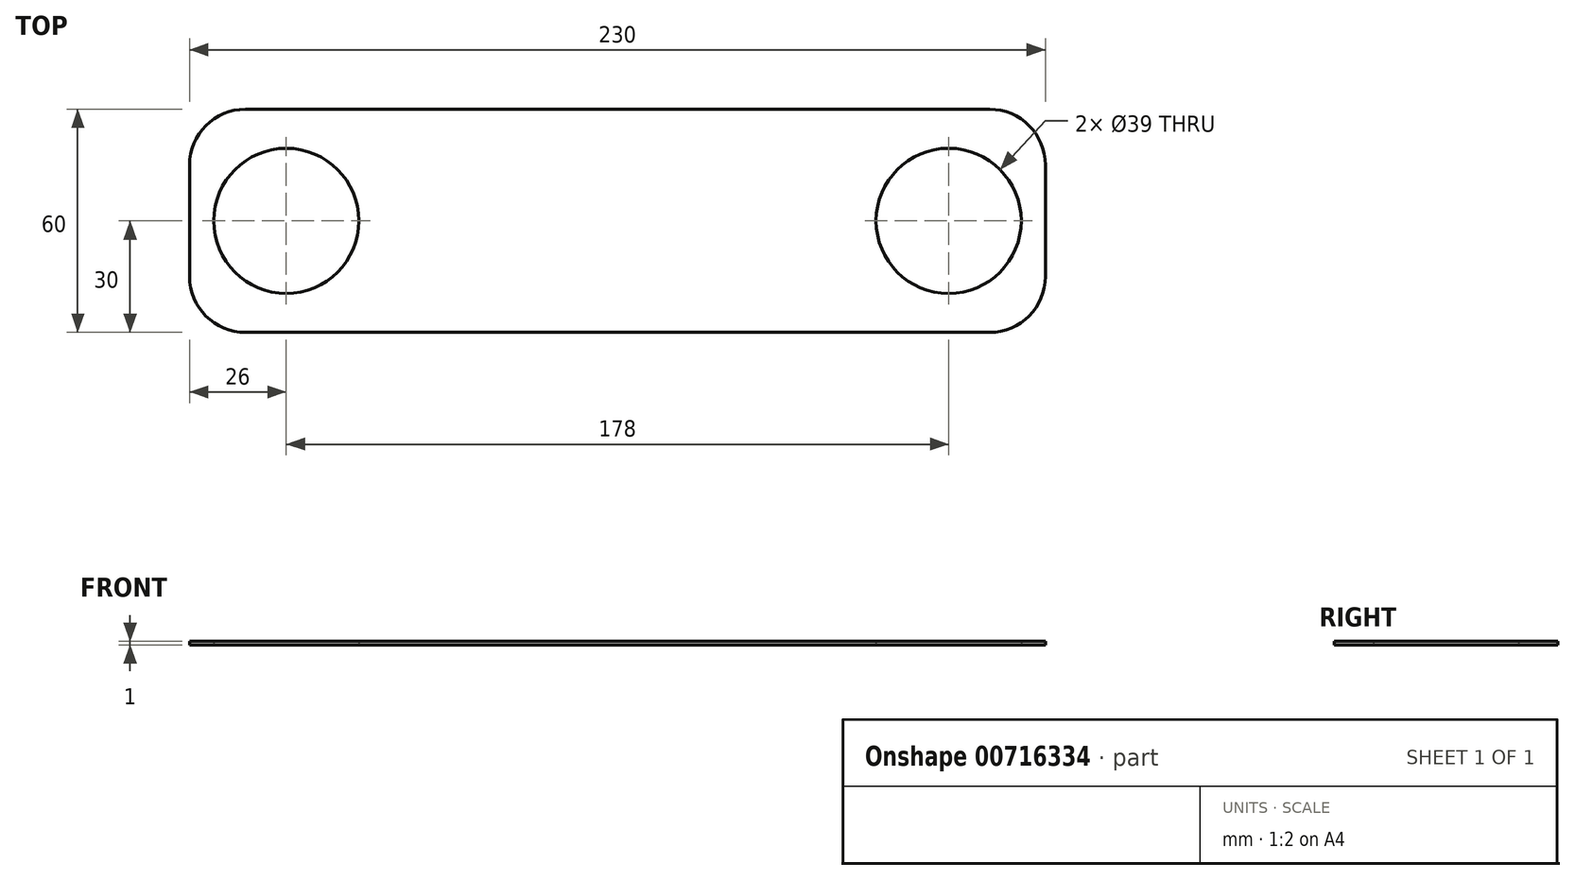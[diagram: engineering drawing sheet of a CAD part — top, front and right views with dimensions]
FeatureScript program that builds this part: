
annotation { "Feature Type Name" : "Feature", "Feature Type Description" : "" }
export const myFeature = defineFeature(function(context is Context, id is Id, definition is map)
    precondition{}
    {
        {
            var Q0;
            Q0=qCreatedBy(makeId("Top.planeOp"),FACE);
            var sketch = newSketch(context, id + "F0", { "sketchPlane" : qUnion([Q0])});
            skLineSegment(sketch, "E0.bottom", {"start": v(100, -30) * mm, "end": v(-100, -30) * mm});
            skLineSegment(sketch, "E0.top", {"start": v(100, 30) * mm, "end": v(-100, 30) * mm});
            skLineSegment(sketch, "E0.left", {"start": v(115, -15) * mm, "end": v(115, 15) * mm});
            skLineSegment(sketch, "E0.right", {"start": v(-115, -15) * mm, "end": v(-115, 15) * mm});
            skPoint(sketch, "E0.middle", {"position": v(0, 0) * mm});
            skLineSegment(sketch, "E1", {"start": v(0, 0) * mm, "end": v(-98.84, 0) * mm, "construction": true});
            skPoint(sketch, "E1.endSnap0", {"position": v(-89, 0) * mm});
            skLineSegment(sketch, "E2", {"start": v(-98.84, 0) * mm, "end": v(125.7, 0) * mm, "construction": true});
            skPoint(sketch, "E3.visualSharp", {"position": v(-115, 30) * mm});
            skArc(sketch, "E3.filletArc", {"start": v(-100, 30) * mm, "mid": v(-110.6, 25.6) * mm, "end": v(-115, 15) * mm});
            skPoint(sketch, "E4.visualSharp", {"position": v(-115, -30) * mm});
            skArc(sketch, "E4.filletArc", {"start": v(-115, -15) * mm, "mid": v(-110.6, -25.6) * mm, "end": v(-100, -30) * mm});
            skPoint(sketch, "E5.visualSharp", {"position": v(115, 30) * mm});
            skArc(sketch, "E5.filletArc", {"start": v(115, 15) * mm, "mid": v(110.6, 25.6) * mm, "end": v(100, 30) * mm});
            skPoint(sketch, "E6.visualSharp", {"position": v(115, -30) * mm});
            skArc(sketch, "E6.filletArc", {"start": v(100, -30) * mm, "mid": v(110.6, -25.6) * mm, "end": v(115, -15) * mm});
            skCircle(sketch, "E7", {"center": v(-89, 0) * mm, "radius": 19.5 * mm});
            skCircle(sketch, "E8", {"center": v(89, 0) * mm, "radius": 19.5 * mm});
            skSolve(sketch);
        }
        {
            var Q0;
            Q0 = qSketchRegion(id + "F0", true);
            extrude(context, id + "F1", {"entities" : qUnion([Q0]), "depth" : 1 * mm, "offsetDistance" : 25 * mm});
        }
    });
